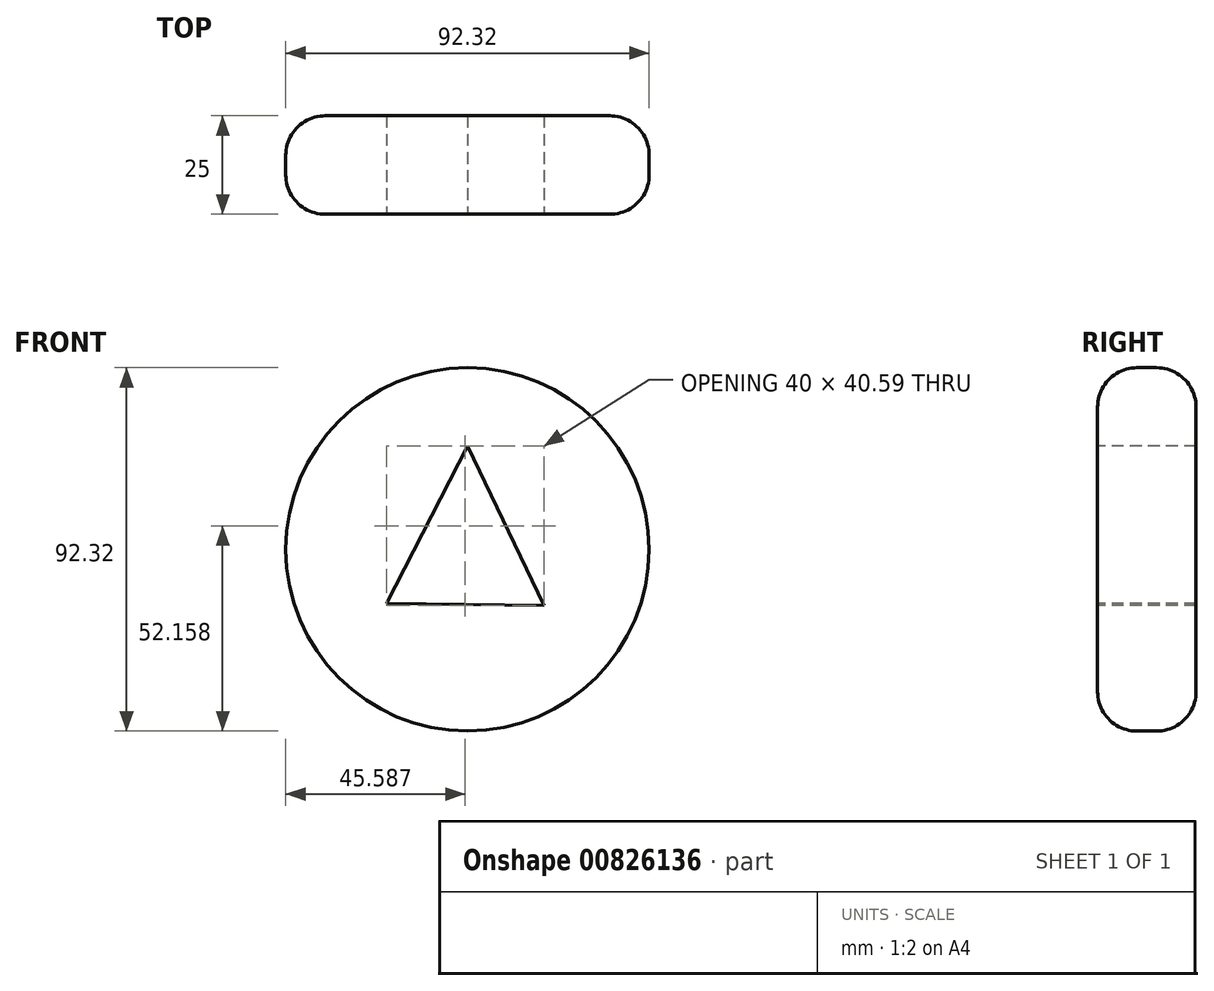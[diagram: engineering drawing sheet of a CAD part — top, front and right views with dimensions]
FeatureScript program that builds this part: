
annotation { "Feature Type Name" : "Feature", "Feature Type Description" : "" }
export const myFeature = defineFeature(function(context is Context, id is Id, definition is map)
    precondition{}
    {
        {
            var Q0;
            Q0=qCreatedBy(makeId("Front.planeOp"),FACE);
            var sketch = newSketch(context, id + "F0", { "sketchPlane" : qUnion([Q0])});
            skCircle(sketch, "E0", {"center": v(0, 0) * mm, "radius": 46.16 * mm});
            skSolve(sketch);
        }
        {
            var Q0;
            Q0 = qSketchRegion(id + "F0", true);
            extrude(context, id + "F1", {"entities" : qUnion([Q0]), "depth" : 25 * mm, "offsetDistance" : 25 * mm});
        }
        {
            var Q0;
            Q0=makeQuery(id+"F1.opExtrude","CAP_FACE",FACE,{"disambiguationData":[OSD([sQuery(id+"F0.wireOp",EDGE,"E0")])],"isStart":false});
            var sketch = newSketch(context, id + "F2", { "sketchPlane" : qUnion([Q0])});
            skLineSegment(sketch, "E1", {"start": v(-20.57, -13.73) * mm, "end": v(0, 26.3) * mm});
            skLineSegment(sketch, "E2", {"start": v(0, 26.3) * mm, "end": v(19.42, -14.3) * mm});
            skLineSegment(sketch, "E3", {"start": v(19.42, -14.3) * mm, "end": v(-20.57, -13.73) * mm});
            skSolve(sketch);
        }
        {
            var Q0;
            Q0 = qSketchRegion(id + "F2", true);
            extrude(context, id + "F3", {"entities" : qUnion([Q0]), "operationType" : NewBodyOperationType.REMOVE, "surfaceOperationType" : NewSurfaceOperationType.ADD, "oppositeDirection" : true, "depth" : 25 * mm, "offsetDistance" : 25 * mm});
        }
        {
            var Q0;
            Q0=makeQuery(id+"F1.opExtrude","CAP_EDGE",EDGE,{"disambiguationData":[OSD([sQuery(id+"F0.wireOp",EDGE,"E0")])],"isStart":false});
            var Q1;
            Q1=makeQuery(id+"F1.opExtrude","CAP_EDGE",EDGE,{"disambiguationData":[OSD([sQuery(id+"F0.wireOp",EDGE,"E0")])],"isStart":true});
            fillet(context, id + "F4", {"entities" : qUnion([Q0, Q1]), "radius" : 10 * mm, "tangentPropagation" : true, "allowEdgeOverflow" : false});
        }
    });
